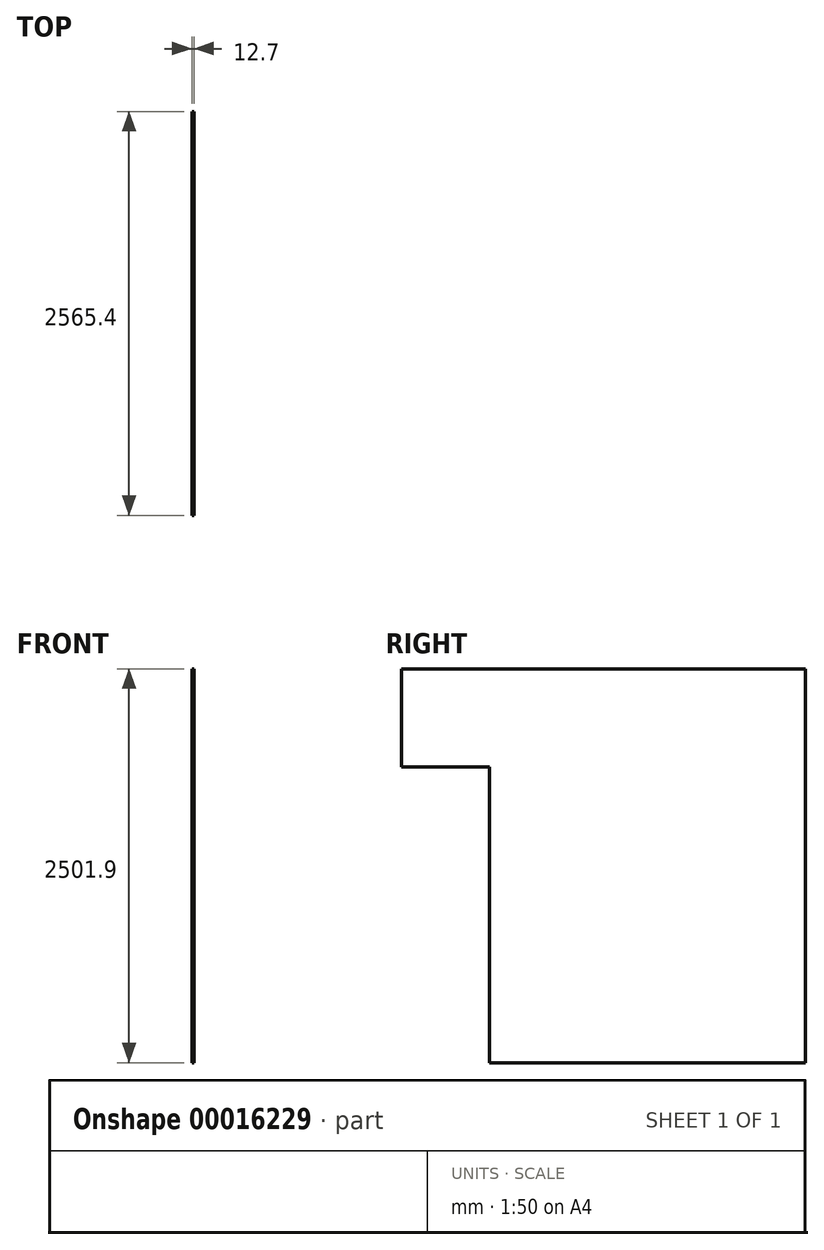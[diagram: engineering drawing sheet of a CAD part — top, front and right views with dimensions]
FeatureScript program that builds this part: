
annotation { "Feature Type Name" : "Feature", "Feature Type Description" : "" }
export const myFeature = defineFeature(function(context is Context, id is Id, definition is map)
    precondition{}
    {
        {
            var Q0;
            Q0=qCreatedBy(makeId("Right.planeOp"),FACE);
            var sketch = newSketch(context, id + "F0", { "sketchPlane" : qUnion([Q0])});
            skLineSegment(sketch, "E0.bottom", {"start": v(-1282.7, 1250.95) * mm, "end": v(1282.7, 1250.95) * mm});
            skLineSegment(sketch, "E0.top", {"start": v(-723.9, -1250.95) * mm, "end": v(1282.7, -1250.95) * mm});
            skLineSegment(sketch, "E0.right", {"start": v(1282.7, 1250.95) * mm, "end": v(1282.7, -1250.95) * mm});
            skPoint(sketch, "E1", {"position": v(1282.7, 0) * mm});
            skPoint(sketch, "E2", {"position": v(0, 1250.95) * mm});
            skLineSegment(sketch, "E3", {"start": v(-1282.7, 1250.95) * mm, "end": v(-1282.7, 628.65) * mm});
            skLineSegment(sketch, "E4", {"start": v(-1282.7, 628.65) * mm, "end": v(-723.9, 628.65) * mm});
            skLineSegment(sketch, "E5", {"start": v(-723.9, 628.65) * mm, "end": v(-723.9, -1250.95) * mm});
            skSolve(sketch);
        }
        {
            var Q0;
            Q0=makeQuery(id+"F0.imprint","IMPRINT",FACE,{"disambiguationData":[TD([[makeQuery(id+"F0.imprint","IMPRINT",EDGE,{"derivedFrom":sQuery(id+"F0.wireOp",EDGE,"E0.bottom")}),-1.0]])]});
            extrude(context, id + "F1", {"entities" : qUnion([Q0]), "depth" : 12.7 * mm});
        }
    });
